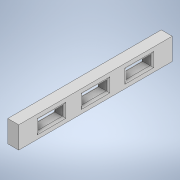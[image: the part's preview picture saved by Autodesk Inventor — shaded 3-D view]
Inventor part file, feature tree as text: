
AUTODESK INVENTOR PART (.ipt)
format: ipt  version: 2020 (Build 240168000, 168)  size: 158,208 bytes
history: native  units: mm
features: extrude x2, sketch x2, fillet x1
ambient origin geometry x8: Origin, YZ Plane, XZ Plane, XY Plane, X Axis, Y Axis, Z Axis, Center Point
bodies: Solid1 (feature_tree)
feature tree (5):
  extrude  "Extrusion1"  Depth=42.0mm
  extrude  "Extrusion2"  TaperAngle=0.0deg  [1 undecoded]
  fillet  "Fillet1"  Radius=6.85mm
  sketch  "Sketch1"  dims[d0=6.0mm d1=42.0mm]
  sketch  "Sketch2"  dims[d2=3.0mm d3=0.0mm d4=6.85mm d5=2.85mm d6=5.575mm d7=30.0mm d9=12.0mm d10=10.0mm d12=10.0mm d14=3.0mm d15=0.0mm d16=5.575mm d17=0.5mm]
note: 1 required parameter value undecoded (feature->parameter linkage not recoverable at this tier; creation-order binding heuristic only, values carry confidence <= 0.55)
